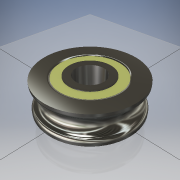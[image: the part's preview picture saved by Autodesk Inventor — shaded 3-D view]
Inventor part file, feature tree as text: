
AUTODESK INVENTOR PART (.ipt)
format: ipt  version: 2016 SP1 (Build 200210100, 210)  size: 208,896 bytes
history: native  units: mm
features: fillet x2, sketch x2, revolve x1, plane x1, extrude x1, mirror x1
ambient origin geometry x8: Origin, YZ Plane, XZ Plane, XY Plane, X Axis, Y Axis, Z Axis, Center Point
bodies: Solid1 (feature_tree)
feature tree (8):
  revolve  "Revolution1"  [1 undecoded]
  plane  "Work Plane1"
  extrude  "Extrusion1"  TaperAngle=90.0deg  [1 undecoded]
  fillet  "Fillet1"  [1 undecoded]
  mirror  "Mirror1"
  fillet  "Fillet2"  Radius=6.0mm
  sketch  "Sketch1"  dims[d0=4.5mm d2=2.0mm]
  sketch  "Sketch2"  dims[d3=2.5mm d4=90.0deg d5=0.0mm d6=6.0mm d7=8.5mm d8=0.1mm d9=0.0mm d14=0.5mm d15=0.5mm]
note: 3 required parameter values undecoded (feature->parameter linkage not recoverable at this tier; creation-order binding heuristic only, values carry confidence <= 0.55)